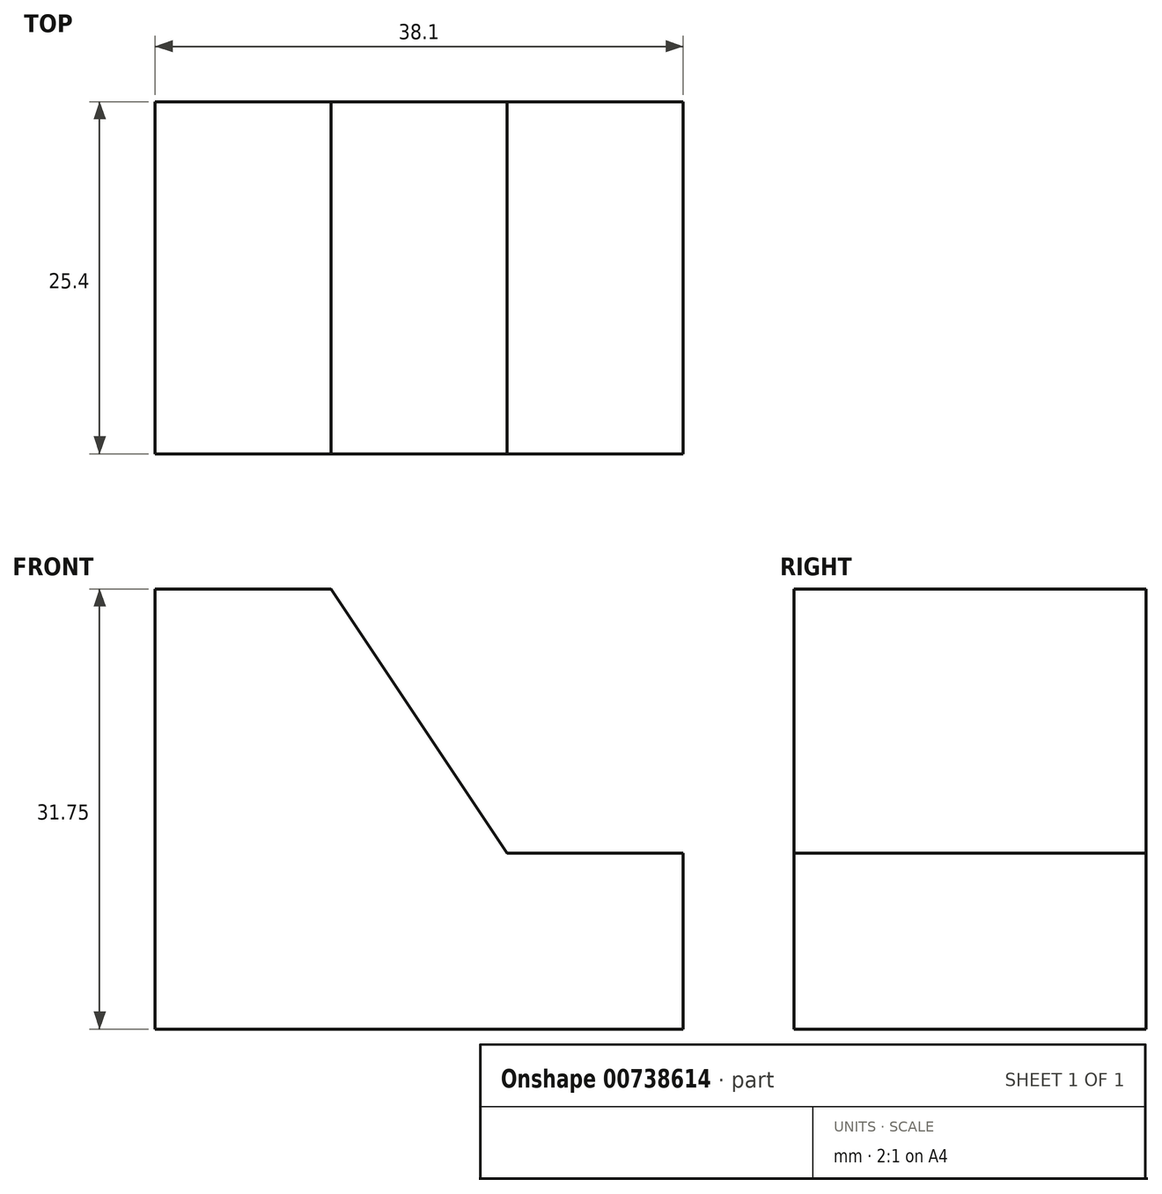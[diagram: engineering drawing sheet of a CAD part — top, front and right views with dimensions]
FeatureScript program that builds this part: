
annotation { "Feature Type Name" : "Feature", "Feature Type Description" : "" }
export const myFeature = defineFeature(function(context is Context, id is Id, definition is map)
    precondition{}
    {
        {
            var Q0;
            Q0=qCreatedBy(makeId("Top.planeOp"),FACE);
            var sketch = newSketch(context, id + "F0", { "sketchPlane" : qUnion([Q0])});
            skLineSegment(sketch, "E0.bottom", {"start": v(0, 0) * mm, "end": v(38.1, 0) * mm});
            skLineSegment(sketch, "E0.top", {"start": v(0, 25.4) * mm, "end": v(38.1, 25.4) * mm});
            skLineSegment(sketch, "E0.left", {"start": v(0, 0) * mm, "end": v(0, 25.4) * mm});
            skLineSegment(sketch, "E0.right", {"start": v(38.1, 0) * mm, "end": v(38.1, 25.4) * mm});
            skSolve(sketch);
        }
        {
            var Q0;
            Q0=makeQuery(id+"F0.imprint","IMPRINT",FACE,{"disambiguationData":[TD([[makeQuery(id+"F0.imprint","IMPRINT",EDGE,{"derivedFrom":sQuery(id+"F0.wireOp",EDGE,"E0.bottom")}),1.0]])]});
            extrude(context, id + "F1", {"entities" : qUnion([Q0]), "depth" : 31.75 * mm, "offsetDistance" : 25.4 * mm});
        }
        {
            var Q0;
            Q0=makeQuery(id+"F1.opExtrude","SWEPT_FACE",FACE,{"disambiguationData":[OSD([sQuery(id+"F0.wireOp",EDGE,"E0.bottom")])]});
            var sketch = newSketch(context, id + "F2", { "sketchPlane" : qUnion([Q0])});
            skLineSegment(sketch, "E1", {"start": v(0, 31.75) * mm, "end": v(12.7, 31.75) * mm});
            skLineSegment(sketch, "E2", {"start": v(38.1, 0) * mm, "end": v(38.1, 12.7) * mm});
            skLineSegment(sketch, "E3", {"start": v(38.1, 12.7) * mm, "end": v(25.4, 12.7) * mm});
            skLineSegment(sketch, "E4", {"start": v(25.4, 12.7) * mm, "end": v(12.7, 31.75) * mm});
            skSolve(sketch);
        }
        {
            var Q0;
            {var subQ0=sQuery(id+"F2.wireOp",EDGE,"E3");Q0=makeQuery(id+"F2.imprint","IMPRINT",FACE,{"disambiguationData":[TD([[makeQuery(id+"F2.imprint","IMPRINT",EDGE,{"derivedFrom":subQ0}),-1.0]])]});}
            extrude(context, id + "F3", {"entities" : qUnion([Q0]), "operationType" : NewBodyOperationType.REMOVE, "oppositeDirection" : true, "depth" : 25.4 * mm, "offsetDistance" : 25.4 * mm});
        }
    });
